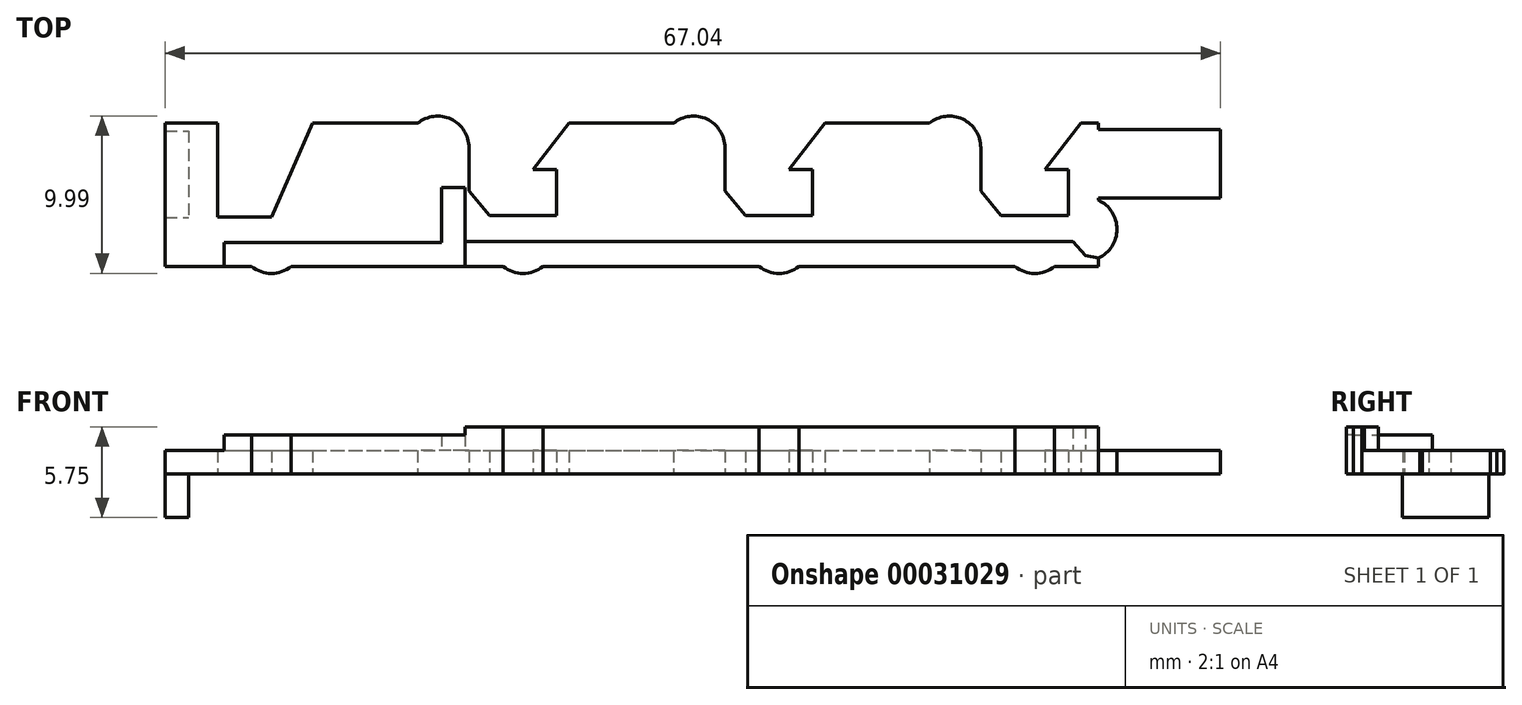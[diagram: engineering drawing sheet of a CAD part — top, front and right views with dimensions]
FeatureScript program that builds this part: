
annotation { "Feature Type Name" : "Feature", "Feature Type Description" : "" }
export const myFeature = defineFeature(function(context is Context, id is Id, definition is map)
    precondition{}
    {
        {
            var Q0;
            Q0=qCreatedBy(makeId("Top.planeOp"),FACE);
            var sketch = newSketch(context, id + "F0", { "sketchPlane" : qUnion([Q0])});
            skLineSegment(sketch, "E0.bottom", {"start": v(-34.84, -0.61) * mm, "end": v(-31.52, -0.61) * mm});
            skLineSegment(sketch, "E0.top", {"start": v(-34.84, -9.7) * mm, "end": v(-29.35, -9.7) * mm});
            skLineSegment(sketch, "E0.left", {"start": v(-34.84, -0.61) * mm, "end": v(-34.84, -9.7) * mm});
            skLineSegment(sketch, "E0.right", {"start": v(32.2, -1.02) * mm, "end": v(32.2, -5.35) * mm});
            skPoint(sketch, "E1", {"position": v(-31.52, -0.61) * mm});
            skLineSegment(sketch, "E2", {"start": v(-31.52, -0.61) * mm, "end": v(-31.52, -6.58) * mm});
            skLineSegment(sketch, "E3", {"start": v(-31.52, -6.58) * mm, "end": v(-28.07, -6.58) * mm});
            skLineSegment(sketch, "E4", {"start": v(-28.07, -6.58) * mm, "end": v(-25.49, -0.61) * mm});
            skLineSegment(sketch, "E5.trimOffspring", {"start": v(-25.49, -0.61) * mm, "end": v(-18.8, -0.61) * mm});
            skLineSegment(sketch, "E6", {"start": v(-15.54, -2.16) * mm, "end": v(-15.54, -4.92) * mm});
            skLineSegment(sketch, "E7", {"start": v(-15.54, -4.92) * mm, "end": v(-14.24, -6.47) * mm});
            skLineSegment(sketch, "E8", {"start": v(-14.24, -6.47) * mm, "end": v(-9.97, -6.47) * mm});
            skLineSegment(sketch, "E9", {"start": v(-9.97, -6.47) * mm, "end": v(-9.97, -3.54) * mm});
            skLineSegment(sketch, "E10", {"start": v(-9.97, -3.54) * mm, "end": v(-11.47, -3.54) * mm});
            skLineSegment(sketch, "E11", {"start": v(-11.47, -3.54) * mm, "end": v(-9.18, -0.61) * mm});
            skLineSegment(sketch, "E12.trimOffspring", {"start": v(-9.18, -0.61) * mm, "end": v(-2.55, -0.61) * mm});
            skLineSegment(sketch, "E13", {"start": v(-42.33, -0.16) * mm, "end": v(54.94, -0.16) * mm, "construction": true});
            skArc(sketch, "E14", {"start": v(-15.54, -2.16) * mm, "mid": v(-16.68, -0.36) * mm, "end": v(-18.8, -0.61) * mm});
            skPoint(sketch, "E15.visualSharp", {"position": v(-11.47, -3.54) * mm});
            skLineSegment(sketch, "E15.filletArc", {"start": v(-11.47, -3.54) * mm, "end": v(-11.47, -3.54) * mm});
            skPoint(sketch, "E16.1.0.0", {"position": v(4.78, -3.54) * mm});
            skLineSegment(sketch, "E16.1.0.1", {"start": v(6.28, -6.47) * mm, "end": v(6.28, -3.54) * mm});
            skLineSegment(sketch, "E16.1.0.2", {"start": v(0.71, -4.92) * mm, "end": v(2.01, -6.47) * mm});
            skLineSegment(sketch, "E16.1.0.3", {"start": v(2.01, -6.47) * mm, "end": v(6.28, -6.47) * mm});
            skLineSegment(sketch, "E16.1.0.4", {"start": v(4.78, -3.54) * mm, "end": v(7.07, -0.61) * mm});
            skLineSegment(sketch, "E16.1.0.5", {"start": v(0.71, -2.16) * mm, "end": v(0.71, -4.92) * mm});
            skArc(sketch, "E16.1.0.6", {"start": v(0.71, -2.16) * mm, "mid": v(-0.43, -0.36) * mm, "end": v(-2.55, -0.61) * mm});
            skLineSegment(sketch, "E16.1.0.7", {"start": v(4.78, -3.54) * mm, "end": v(4.78, -3.54) * mm});
            skLineSegment(sketch, "E16.1.0.8", {"start": v(6.28, -3.54) * mm, "end": v(4.78, -3.54) * mm});
            skPoint(sketch, "E16.2.0.0", {"position": v(21.03, -3.54) * mm});
            skLineSegment(sketch, "E16.2.0.1", {"start": v(22.53, -6.47) * mm, "end": v(22.53, -3.54) * mm});
            skLineSegment(sketch, "E16.2.0.2", {"start": v(16.96, -4.92) * mm, "end": v(18.26, -6.47) * mm});
            skLineSegment(sketch, "E16.2.0.3", {"start": v(18.26, -6.47) * mm, "end": v(22.53, -6.47) * mm});
            skLineSegment(sketch, "E16.2.0.4", {"start": v(21.03, -3.54) * mm, "end": v(23.32, -0.61) * mm});
            skLineSegment(sketch, "E16.2.0.5", {"start": v(16.96, -2.16) * mm, "end": v(16.96, -4.92) * mm});
            skArc(sketch, "E16.2.0.6", {"start": v(16.96, -2.16) * mm, "mid": v(15.82, -0.36) * mm, "end": v(13.7, -0.61) * mm});
            skLineSegment(sketch, "E16.2.0.7", {"start": v(21.03, -3.54) * mm, "end": v(21.03, -3.54) * mm});
            skLineSegment(sketch, "E16.2.0.8", {"start": v(22.53, -3.54) * mm, "end": v(21.03, -3.54) * mm});
            skLineSegment(sketch, "E16.direction1", {"start": v(-11.47, -3.54) * mm, "end": v(4.78, -3.54) * mm, "construction": true});
            skLineSegment(sketch, "E17.trimOffspring", {"start": v(7.07, -0.61) * mm, "end": v(13.7, -0.61) * mm});
            skLineSegment(sketch, "E18.trimOffspring", {"start": v(23.32, -0.61) * mm, "end": v(24.43, -0.61) * mm});
            skPoint(sketch, "E19", {"position": v(32.2, -5.35) * mm});
            skPoint(sketch, "E20", {"position": v(32.2, -1.02) * mm});
            skPoint(sketch, "E21", {"position": v(24.43, -9.7) * mm});
            skPoint(sketch, "E22", {"position": v(24.43, -0.61) * mm});
            skLineSegment(sketch, "E23", {"start": v(24.43, -9.7) * mm, "end": v(24.43, -9.18) * mm});
            skLineSegment(sketch, "E24", {"start": v(32.2, -5.35) * mm, "end": v(24.43, -5.35) * mm});
            skLineSegment(sketch, "E25", {"start": v(24.43, -0.61) * mm, "end": v(24.43, -1.02) * mm});
            skLineSegment(sketch, "E26", {"start": v(32.2, -1.02) * mm, "end": v(24.43, -1.02) * mm});
            skArc(sketch, "E27", {"start": v(24.43, -9.18) * mm, "mid": v(25.62, -7.34) * mm, "end": v(24.43, -5.5) * mm});
            skLineSegment(sketch, "E28.trimOffspring", {"start": v(24.43, -5.5) * mm, "end": v(24.43, -5.35) * mm});
            skLineSegment(sketch, "E29", {"start": v(-43.1, -10.15) * mm, "end": v(46.08, -10.15) * mm, "construction": true});
            skPoint(sketch, "E30", {"position": v(-12.1, -6.47) * mm});
            skPoint(sketch, "E31", {"position": v(4.15, -6.47) * mm});
            skPoint(sketch, "E32", {"position": v(20.4, -6.47) * mm});
            skLineSegment(sketch, "E33", {"start": v(-12.1, -6.47) * mm, "end": v(-12.1, -17.32) * mm, "construction": true});
            skLineSegment(sketch, "E34", {"start": v(20.4, -6.47) * mm, "end": v(20.4, -16.54) * mm, "construction": true});
            skLineSegment(sketch, "E35", {"start": v(4.15, -6.47) * mm, "end": v(4.15, -16.95) * mm, "construction": true});
            skArc(sketch, "E36", {"start": v(-13.37, -9.7) * mm, "mid": v(-12.1, -10.15) * mm, "end": v(-10.84, -9.7) * mm});
            skLineSegment(sketch, "E37", {"start": v(-12.1, -8.15) * mm, "end": v(42.97, -8.15) * mm, "construction": true});
            skArc(sketch, "E38", {"start": v(2.88, -9.7) * mm, "mid": v(4.15, -10.15) * mm, "end": v(5.41, -9.7) * mm});
            skArc(sketch, "E39", {"start": v(19.13, -9.7) * mm, "mid": v(20.4, -10.15) * mm, "end": v(21.66, -9.7) * mm});
            skLineSegment(sketch, "E40.trimOffspring", {"start": v(-10.84, -9.7) * mm, "end": v(2.88, -9.7) * mm});
            skLineSegment(sketch, "E41.trimOffspring", {"start": v(5.41, -9.7) * mm, "end": v(19.13, -9.7) * mm});
            skLineSegment(sketch, "E42.trimOffspring", {"start": v(21.66, -9.7) * mm, "end": v(24.43, -9.7) * mm});
            skLineSegment(sketch, "E43", {"start": v(-12.1, -8.15) * mm, "end": v(-39.1, -8.15) * mm, "construction": true});
            skArc(sketch, "E44", {"start": v(-29.35, -9.7) * mm, "mid": v(-28.09, -10.15) * mm, "end": v(-26.83, -9.7) * mm});
            skLineSegment(sketch, "E45.trimOffspring", {"start": v(-26.83, -9.7) * mm, "end": v(-13.37, -9.7) * mm});
            skSolve(sketch);
        }
        {
            var Q0;
            Q0=qSketchRegion(id+"F0",true);
            extrude(context, id + "F1", {"entities" : qUnion([Q0]), "depth" : 1.5 * mm});
        }
        {
            var Q0;
            Q0=makeQuery(id+"F1.opExtrude","CAP_FACE",FACE,{"disambiguationData":[OSD([sQuery(id+"F0.wireOp",EDGE,"E0.bottom"),sQuery(id+"F0.wireOp",EDGE,"E0.top"),sQuery(id+"F0.wireOp",EDGE,"E0.left"),sQuery(id+"F0.wireOp",EDGE,"E0.right"),sQuery(id+"F0.wireOp",EDGE,"E2"),sQuery(id+"F0.wireOp",EDGE,"E3"),sQuery(id+"F0.wireOp",EDGE,"E4"),sQuery(id+"F0.wireOp",EDGE,"E5.trimOffspring"),sQuery(id+"F0.wireOp",EDGE,"E6"),sQuery(id+"F0.wireOp",EDGE,"E7"),sQuery(id+"F0.wireOp",EDGE,"E8"),sQuery(id+"F0.wireOp",EDGE,"E9"),sQuery(id+"F0.wireOp",EDGE,"E10"),sQuery(id+"F0.wireOp",EDGE,"E11"),sQuery(id+"F0.wireOp",EDGE,"E12.trimOffspring"),sQuery(id+"F0.wireOp",EDGE,"E14"),sQuery(id+"F0.wireOp",EDGE,"E15.filletArc"),sQuery(id+"F0.wireOp",EDGE,"E16.1.0.1"),sQuery(id+"F0.wireOp",EDGE,"E16.1.0.2"),sQuery(id+"F0.wireOp",EDGE,"E16.1.0.3"),sQuery(id+"F0.wireOp",EDGE,"E16.1.0.4"),sQuery(id+"F0.wireOp",EDGE,"E16.1.0.5"),sQuery(id+"F0.wireOp",EDGE,"E16.1.0.6"),sQuery(id+"F0.wireOp",EDGE,"E16.1.0.7"),sQuery(id+"F0.wireOp",EDGE,"E16.1.0.8"),sQuery(id+"F0.wireOp",EDGE,"E16.2.0.1"),sQuery(id+"F0.wireOp",EDGE,"E16.2.0.2"),sQuery(id+"F0.wireOp",EDGE,"E16.2.0.3"),sQuery(id+"F0.wireOp",EDGE,"E16.2.0.4"),sQuery(id+"F0.wireOp",EDGE,"E16.2.0.5"),sQuery(id+"F0.wireOp",EDGE,"E16.2.0.6"),sQuery(id+"F0.wireOp",EDGE,"E16.2.0.7"),sQuery(id+"F0.wireOp",EDGE,"E16.2.0.8"),sQuery(id+"F0.wireOp",EDGE,"E17.trimOffspring"),sQuery(id+"F0.wireOp",EDGE,"E18.trimOffspring"),sQuery(id+"F0.wireOp",EDGE,"E23"),sQuery(id+"F0.wireOp",EDGE,"E24"),sQuery(id+"F0.wireOp",EDGE,"E25"),sQuery(id+"F0.wireOp",EDGE,"E26"),sQuery(id+"F0.wireOp",EDGE,"E27"),sQuery(id+"F0.wireOp",EDGE,"E28.trimOffspring"),sQuery(id+"F0.wireOp",EDGE,"E36"),sQuery(id+"F0.wireOp",EDGE,"E38"),sQuery(id+"F0.wireOp",EDGE,"E39"),sQuery(id+"F0.wireOp",EDGE,"E40.trimOffspring"),sQuery(id+"F0.wireOp",EDGE,"E41.trimOffspring"),sQuery(id+"F0.wireOp",EDGE,"E42.trimOffspring"),sQuery(id+"F0.wireOp",EDGE,"E44"),sQuery(id+"F0.wireOp",EDGE,"E45.trimOffspring")])],"isStart":false});
            var sketch = newSketch(context, id + "F2", { "sketchPlane" : qUnion([Q0])});
            skLineSegment(sketch, "E46.0", {"start": v(-31.09, -9.7) * mm, "end": v(-29.35, -9.7) * mm});
            skArc(sketch, "E46.1", {"start": v(-29.35, -9.7) * mm, "mid": v(-28.09, -10.15) * mm, "end": v(-26.83, -9.7) * mm});
            skLineSegment(sketch, "E46.2", {"start": v(-26.83, -9.7) * mm, "end": v(-13.37, -9.7) * mm});
            skArc(sketch, "E46.3", {"start": v(-13.37, -9.7) * mm, "mid": v(-12.1, -10.15) * mm, "end": v(-10.84, -9.7) * mm});
            skLineSegment(sketch, "E46.4", {"start": v(-10.84, -9.7) * mm, "end": v(2.88, -9.7) * mm});
            skArc(sketch, "E46.5", {"start": v(2.88, -9.7) * mm, "mid": v(4.15, -10.15) * mm, "end": v(5.41, -9.7) * mm});
            skLineSegment(sketch, "E46.6", {"start": v(5.41, -9.7) * mm, "end": v(19.13, -9.7) * mm});
            skArc(sketch, "E46.7", {"start": v(19.13, -9.7) * mm, "mid": v(20.4, -10.15) * mm, "end": v(21.66, -9.7) * mm});
            skLineSegment(sketch, "E46.8", {"start": v(21.66, -9.7) * mm, "end": v(24.43, -9.7) * mm});
            skPoint(sketch, "E47", {"position": v(-31.09, -9.7) * mm});
            skLineSegment(sketch, "E48", {"start": v(-31.09, -9.7) * mm, "end": v(-31.09, -8.2) * mm});
            skLineSegment(sketch, "E49", {"start": v(-31.09, -8.2) * mm, "end": v(-17.29, -8.2) * mm});
            skLineSegment(sketch, "E50", {"start": v(-15.79, -4.7) * mm, "end": v(-15.79, -8.13) * mm});
            skLineSegment(sketch, "E51", {"start": v(-15.79, -4.7) * mm, "end": v(-17.29, -4.7) * mm});
            skLineSegment(sketch, "E52", {"start": v(-17.29, -4.7) * mm, "end": v(-17.29, -8.2) * mm});
            skLineSegment(sketch, "E53", {"start": v(-15.79, -8.13) * mm, "end": v(22.8, -8.13) * mm});
            skLineSegment(sketch, "E54", {"start": v(22.8, -8.13) * mm, "end": v(23.6, -9.02) * mm});
            skLineSegment(sketch, "E55", {"start": v(23.6, -9.02) * mm, "end": v(24.43, -9.18) * mm});
            skLineSegment(sketch, "E56", {"start": v(24.43, -9.18) * mm, "end": v(24.43, -9.7) * mm});
            skPoint(sketch, "E57.orphan", {"position": v(-15.79, -9.7) * mm});
            skSolve(sketch);
        }
        {
            var Q0;
            Q0=makeQuery(id+"F2.imprint","IMPRINT",FACE,{"disambiguationData":[TD([[makeQuery(id+"F2.imprint","IMPRINT",EDGE,{"derivedFrom":sQuery(id+"F2.wireOp",EDGE,"E46.0")}),1.0]])]});
            extrude(context, id + "F3", {"entities" : qUnion([Q0]), "operationType" : NewBodyOperationType.ADD, "depth" : 1.5 * mm});
        }
        {
            var Q0;
            Q0=makeQuery(id+"F3.opExtrude","SWEPT_FACE",FACE,{"disambiguationData":[OSD([sQuery(id+"F2.wireOp",EDGE,"E49")])]});
            var sketch = newSketch(context, id + "F4", { "sketchPlane" : qUnion([Q0])});
            skLineSegment(sketch, "E58.bottom", {"start": v(31.09, 3) * mm, "end": v(15.78, 3) * mm});
            skLineSegment(sketch, "E58.top", {"start": v(31.09, 2.5) * mm, "end": v(15.78, 2.5) * mm});
            skLineSegment(sketch, "E58.left", {"start": v(31.09, 3) * mm, "end": v(31.09, 2.5) * mm});
            skLineSegment(sketch, "E58.right", {"start": v(15.78, 3) * mm, "end": v(15.78, 2.5) * mm});
            skSolve(sketch);
        }
        {
            var Q0;
            Q0=qSketchRegion(id+"F4",true);
            extrude(context, id + "F5", {"entities" : qUnion([Q0]), "operationType" : NewBodyOperationType.REMOVE, "endBound" : BoundingType.SYMMETRIC, "oppositeDirection" : true, "depth" : 25 * mm});
        }
        {
            var Q0;
            Q0=makeQuery(id+"F1.opExtrude","CAP_FACE",FACE,{"disambiguationData":[OSD([sQuery(id+"F0.wireOp",EDGE,"E0.bottom"),sQuery(id+"F0.wireOp",EDGE,"E0.top"),sQuery(id+"F0.wireOp",EDGE,"E0.left"),sQuery(id+"F0.wireOp",EDGE,"E0.right"),sQuery(id+"F0.wireOp",EDGE,"E2"),sQuery(id+"F0.wireOp",EDGE,"E3"),sQuery(id+"F0.wireOp",EDGE,"E4"),sQuery(id+"F0.wireOp",EDGE,"E5.trimOffspring"),sQuery(id+"F0.wireOp",EDGE,"E6"),sQuery(id+"F0.wireOp",EDGE,"E7"),sQuery(id+"F0.wireOp",EDGE,"E8"),sQuery(id+"F0.wireOp",EDGE,"E9"),sQuery(id+"F0.wireOp",EDGE,"E10"),sQuery(id+"F0.wireOp",EDGE,"E11"),sQuery(id+"F0.wireOp",EDGE,"E12.trimOffspring"),sQuery(id+"F0.wireOp",EDGE,"E14"),sQuery(id+"F0.wireOp",EDGE,"E15.filletArc"),sQuery(id+"F0.wireOp",EDGE,"E16.1.0.1"),sQuery(id+"F0.wireOp",EDGE,"E16.1.0.2"),sQuery(id+"F0.wireOp",EDGE,"E16.1.0.3"),sQuery(id+"F0.wireOp",EDGE,"E16.1.0.4"),sQuery(id+"F0.wireOp",EDGE,"E16.1.0.5"),sQuery(id+"F0.wireOp",EDGE,"E16.1.0.6"),sQuery(id+"F0.wireOp",EDGE,"E16.1.0.7"),sQuery(id+"F0.wireOp",EDGE,"E16.1.0.8"),sQuery(id+"F0.wireOp",EDGE,"E16.2.0.1"),sQuery(id+"F0.wireOp",EDGE,"E16.2.0.2"),sQuery(id+"F0.wireOp",EDGE,"E16.2.0.3"),sQuery(id+"F0.wireOp",EDGE,"E16.2.0.4"),sQuery(id+"F0.wireOp",EDGE,"E16.2.0.5"),sQuery(id+"F0.wireOp",EDGE,"E16.2.0.6"),sQuery(id+"F0.wireOp",EDGE,"E16.2.0.7"),sQuery(id+"F0.wireOp",EDGE,"E16.2.0.8"),sQuery(id+"F0.wireOp",EDGE,"E17.trimOffspring"),sQuery(id+"F0.wireOp",EDGE,"E18.trimOffspring"),sQuery(id+"F0.wireOp",EDGE,"E23"),sQuery(id+"F0.wireOp",EDGE,"E24"),sQuery(id+"F0.wireOp",EDGE,"E25"),sQuery(id+"F0.wireOp",EDGE,"E26"),sQuery(id+"F0.wireOp",EDGE,"E27"),sQuery(id+"F0.wireOp",EDGE,"E28.trimOffspring"),sQuery(id+"F0.wireOp",EDGE,"E36"),sQuery(id+"F0.wireOp",EDGE,"E38"),sQuery(id+"F0.wireOp",EDGE,"E39"),sQuery(id+"F0.wireOp",EDGE,"E40.trimOffspring"),sQuery(id+"F0.wireOp",EDGE,"E41.trimOffspring"),sQuery(id+"F0.wireOp",EDGE,"E42.trimOffspring"),sQuery(id+"F0.wireOp",EDGE,"E44"),sQuery(id+"F0.wireOp",EDGE,"E45.trimOffspring")])],"isStart":true});
            var sketch = newSketch(context, id + "F6", { "sketchPlane" : qUnion([Q0])});
            skLineSegment(sketch, "E59.bottom", {"start": v(-34.84, 1.1) * mm, "end": v(-33.34, 1.1) * mm});
            skLineSegment(sketch, "E59.top", {"start": v(-34.84, 6.61) * mm, "end": v(-33.34, 6.61) * mm});
            skLineSegment(sketch, "E59.left", {"start": v(-34.84, 1.1) * mm, "end": v(-34.84, 6.61) * mm});
            skLineSegment(sketch, "E59.right", {"start": v(-33.34, 1.1) * mm, "end": v(-33.34, 6.61) * mm});
            skSolve(sketch);
        }
        {
            var Q0;
            Q0=qSketchRegion(id+"F6",true);
            extrude(context, id + "F7", {"entities" : qUnion([Q0]), "operationType" : NewBodyOperationType.ADD, "depth" : 2.75 * mm});
        }
    });
